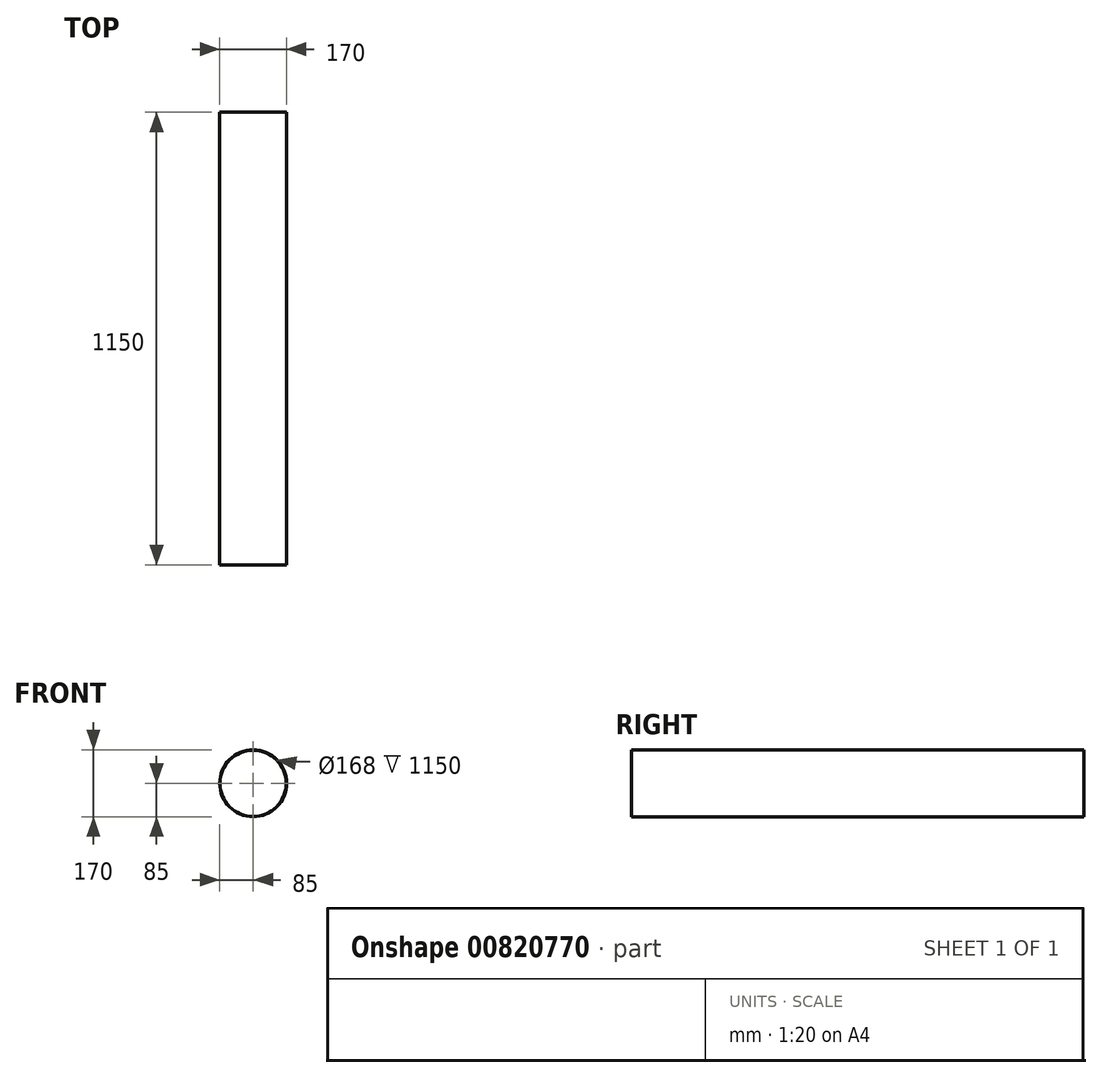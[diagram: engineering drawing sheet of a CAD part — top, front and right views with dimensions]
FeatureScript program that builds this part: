
annotation { "Feature Type Name" : "Feature", "Feature Type Description" : "" }
export const myFeature = defineFeature(function(context is Context, id is Id, definition is map)
    precondition{}
    {
        {
            var Q0;
            Q0=qCreatedBy(makeId("Front.planeOp"),FACE);
            var sketch = newSketch(context, id + "F0", { "sketchPlane" : qUnion([Q0])});
            skCircle(sketch, "E0", {"center": v(0, 0) * mm, "radius": 84 * mm});
            skCircle(sketch, "E1", {"center": v(0, 0) * mm, "radius": 85 * mm});
            skSolve(sketch);
        }
        {
            var Q0;
            Q0=qSketchRegion(id+"F0",true);
            extrude(context, id + "F1", {"entities" : qUnion([Q0]), "depth" : 1150 * mm, "offsetDistance" : 25 * mm});
        }
    });
